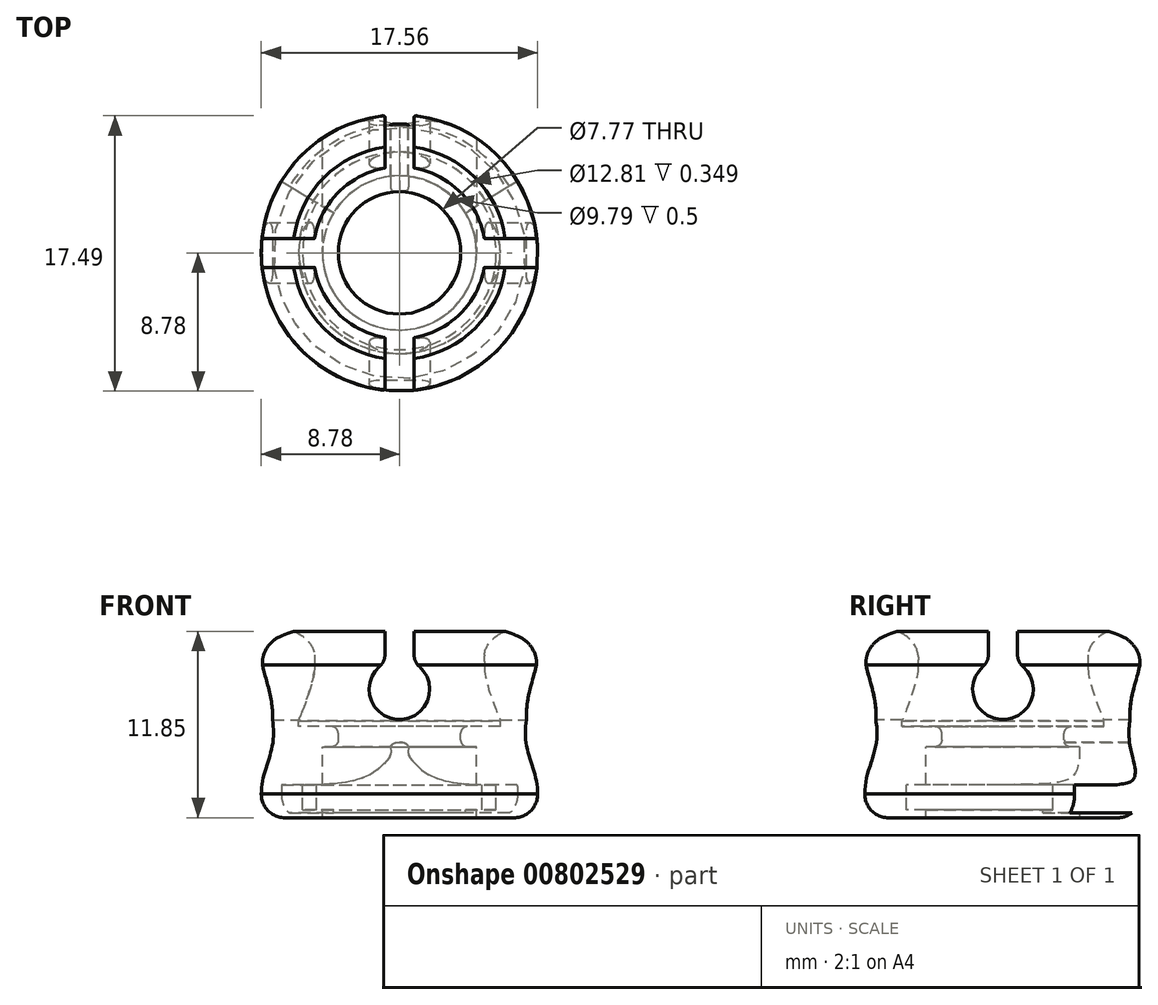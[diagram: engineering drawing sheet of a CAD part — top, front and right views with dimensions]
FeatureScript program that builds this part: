
annotation { "Feature Type Name" : "Feature", "Feature Type Description" : "" }
export const myFeature = defineFeature(function(context is Context, id is Id, definition is map)
    precondition{}
    {
        {
            var Q0;
            Q0=qCreatedBy(makeId("Front.planeOp"),FACE);
            var sketch = newSketch(context, id + "F0", { "sketchPlane" : qUnion([Q0])});
            skLineSegment(sketch, "E0", {"start": v(-3.88, 3.25) * mm, "end": v(-3.88, 2.85) * mm});
            skLineSegment(sketch, "E1", {"start": v(-4.34, 2.4) * mm, "end": v(-4.9, 2.4) * mm});
            skLineSegment(sketch, "E2", {"start": v(-4.9, 2.4) * mm, "end": v(-4.9, 0) * mm});
            skLineSegment(sketch, "E3", {"start": v(-4.9, 0) * mm, "end": v(-6.14, 0) * mm});
            skLineSegment(sketch, "E4", {"start": v(-6.14, 0) * mm, "end": v(-6.14, -1.6) * mm});
            skLineSegment(sketch, "E5", {"start": v(-6.14, -1.6) * mm, "end": v(-4.9, -1.6) * mm});
            skLineSegment(sketch, "E6", {"start": v(-4.9, -1.6) * mm, "end": v(-4.9, -2.1) * mm});
            skLineSegment(sketch, "E7", {"start": v(-4.9, -2.1) * mm, "end": v(-7.28, -2.1) * mm});
            skLineSegment(sketch, "E8", {"start": v(-8.78, -0.6) * mm, "end": v(-8.78, -0.6) * mm});
            skLineSegment(sketch, "E9", {"start": v(-7.47, 9.5) * mm, "end": v(-6.77, 9.75) * mm});
            skLineSegment(sketch, "E10", {"start": v(0, 14.29) * mm, "end": v(0, -15.3) * mm, "construction": true});
            skLineSegment(sketch, "E11", {"start": v(-6.4, 4.05) * mm, "end": v(-6.4, 3.7) * mm});
            skLineSegment(sketch, "E12", {"start": v(-6.4, 3.7) * mm, "end": v(-4.34, 3.7) * mm});
            skPoint(sketch, "E13.visualSharp", {"position": v(-8.78, 9) * mm});
            skArc(sketch, "E13.filletArc", {"start": v(-7.47, 9.5) * mm, "mid": v(-8.42, 8.76) * mm, "end": v(-8.78, 7.62) * mm});
            skPoint(sketch, "E14.visualSharp", {"position": v(-8.78, -2.1) * mm});
            skArc(sketch, "E14.filletArc", {"start": v(-8.78, -0.6) * mm, "mid": v(-8.34, -1.66) * mm, "end": v(-7.28, -2.1) * mm});
            skFitSpline(sketch, "E15", {"points": [v(-8.77, 7.62) * mm, v(-8, 3.1) * mm, v(-8.77, -0.6) * mm], "startDerivative": vector(0.2, -7.43) * mm, "endDerivative": vector(0.17, -8.43) * mm});
            skPoint(sketch, "E16.2.internal.snap0", {"position": v(-5.95, 7.8) * mm});
            skFitSpline(sketch, "E16", {"points": [v(-6.77, 9.75) * mm, v(-5.5, 8.43) * mm, v(-5.95, 6.2) * mm, v(-6.4, 4.05) * mm], "startDerivative": vector(5.68, -2.33) * mm, "endDerivative": vector(-0.9, -5.9) * mm});
            skPoint(sketch, "E17.orphan", {"position": v(-6.4, 7.18) * mm});
            skPoint(sketch, "E18.visualSharp", {"position": v(-3.88, 3.7) * mm});
            skArc(sketch, "E18.filletArc", {"start": v(-3.88, 3.25) * mm, "mid": v(-4.02, 3.57) * mm, "end": v(-4.34, 3.7) * mm});
            skPoint(sketch, "E19.visualSharp", {"position": v(-3.88, 2.4) * mm});
            skArc(sketch, "E19.filletArc", {"start": v(-4.34, 2.4) * mm, "mid": v(-4.02, 2.53) * mm, "end": v(-3.88, 2.85) * mm});
            skSolve(sketch);
        }
        {
            var Q0;
            Q0=qSketchRegion(id+"F0",true);
            var Q1;
            Q1=sQuery(id+"F0.wireOp",EDGE,"E10");
            revolve(context, id + "F1", {"surfaceOperationType" : NewSurfaceOperationType.NEW, "entities" : qUnion([Q0]), "axis" : qUnion([Q1]), "revolveType" : RevolveType.FULL});
        }
        {
            var Q0;
            Q0=qCreatedBy(makeId("Right.planeOp"),FACE);
            var sketch = newSketch(context, id + "F2", { "sketchPlane" : qUnion([Q0])});
            skArc(sketch, "E20", {"start": v(-1.27, 7.5) * mm, "mid": v(0, 4.13) * mm, "end": v(1.27, 7.5) * mm});
            skLineSegment(sketch, "E21.top", {"start": v(-0.92, 15.11) * mm, "end": v(0.93, 15.11) * mm});
            skLineSegment(sketch, "E21.left", {"start": v(-0.92, 8.26) * mm, "end": v(-0.92, 15.11) * mm});
            skLineSegment(sketch, "E21.right", {"start": v(0.93, 8.26) * mm, "end": v(0.93, 15.11) * mm});
            skPoint(sketch, "E21.middle", {"position": v(0, 11.1) * mm});
            skPoint(sketch, "E22.orphan", {"position": v(0.93, 7.1) * mm});
            skPoint(sketch, "E23.orphan", {"position": v(-0.92, 7.1) * mm});
            skPoint(sketch, "E24.visualSharp", {"position": v(0.93, 7.74) * mm});
            skArc(sketch, "E24.filletArc", {"start": v(0.92, 8.26) * mm, "mid": v(1.01, 7.84) * mm, "end": v(1.27, 7.5) * mm});
            skPoint(sketch, "E25.visualSharp", {"position": v(-0.92, 7.74) * mm});
            skArc(sketch, "E25.filletArc", {"start": v(-1.27, 7.5) * mm, "mid": v(-1.01, 7.84) * mm, "end": v(-0.92, 8.26) * mm});
            skSolve(sketch);
        }
        {
            var Q0;
            Q0=qSketchRegion(id+"F2",true);
            extrude(context, id + "F3", {"entities" : qUnion([Q0]), "operationType" : NewBodyOperationType.REMOVE, "endBound" : BoundingType.SYMMETRIC, "oppositeDirection" : true, "depth" : 25 * mm, "offsetDistance" : 25 * mm});
        }
        {
            var Q0;
            Q0=qCreatedBy(makeId("Front.planeOp"),FACE);
            var sketch = newSketch(context, id + "F4", { "sketchPlane" : qUnion([Q0])});
            skArc(sketch, "E26", {"start": v(-1.27, 7.5) * mm, "mid": v(0, 4.13) * mm, "end": v(1.27, 7.5) * mm});
            skLineSegment(sketch, "E27.top", {"start": v(-0.92, 15.11) * mm, "end": v(0.93, 15.11) * mm});
            skLineSegment(sketch, "E27.left", {"start": v(-0.92, 8.26) * mm, "end": v(-0.92, 15.11) * mm});
            skLineSegment(sketch, "E27.right", {"start": v(0.93, 8.26) * mm, "end": v(0.93, 15.11) * mm});
            skPoint(sketch, "E27.middle", {"position": v(0, 11.1) * mm});
            skPoint(sketch, "E28.orphan", {"position": v(0.93, 7.1) * mm});
            skPoint(sketch, "E29.orphan", {"position": v(-0.92, 7.1) * mm});
            skPoint(sketch, "E30.visualSharp", {"position": v(0.93, 7.74) * mm});
            skArc(sketch, "E30.filletArc", {"start": v(0.93, 8.26) * mm, "mid": v(1.01, 7.84) * mm, "end": v(1.27, 7.5) * mm});
            skPoint(sketch, "E31.visualSharp", {"position": v(-0.92, 7.74) * mm});
            skArc(sketch, "E31.filletArc", {"start": v(-1.27, 7.5) * mm, "mid": v(-1.01, 7.84) * mm, "end": v(-0.92, 8.26) * mm});
            skSolve(sketch);
        }
        {
            var Q0;
            Q0=qSketchRegion(id+"F4",true);
            extrude(context, id + "F5", {"entities" : qUnion([Q0]), "operationType" : NewBodyOperationType.REMOVE, "endBound" : BoundingType.SYMMETRIC, "oppositeDirection" : true, "depth" : 25 * mm, "offsetDistance" : 25 * mm});
        }
        {
            var Q0;
            Q0=qCreatedBy(makeId("Front.planeOp"),FACE);
            var sketch = newSketch(context, id + "F6", { "sketchPlane" : qUnion([Q0])});
            skFitSpline(sketch, "E32", {"points": [v(-4.9, 0) * mm, v(-2.89, 0.26) * mm, v(-1.45, 0.92) * mm, v(-0.69, 1.68) * mm, v(-0.54, 2.03) * mm, v(0, 2.68) * mm], "startDerivative": vector(7.16, 0.52) * mm, "endDerivative": vector(12.5, -0.27) * mm});
            skLineSegment(sketch, "E33", {"start": v(-4.9, 0) * mm, "end": v(0, 0) * mm});
            skLineSegment(sketch, "E34", {"start": v(0, 5.3) * mm, "end": v(0, -2.76) * mm, "construction": true});
            skFitSpline(sketch, "E35.MirrorCS", {"points": [v(4.9, 0) * mm, v(2.89, 0.26) * mm, v(1.45, 0.92) * mm, v(0.69, 1.68) * mm, v(0.54, 2.03) * mm, v(0, 2.68) * mm], "startDerivative": vector(-7.16, 0.52) * mm, "endDerivative": vector(-12.5, -0.27) * mm});
            skLineSegment(sketch, "E36.MirrorCS", {"start": v(4.9, 0) * mm, "end": v(0, 0) * mm});
            skSolve(sketch);
        }
        {
            var Q0;
            Q0=qSketchRegion(id+"F6",true);
            extrude(context, id + "F7", {"entities" : qUnion([Q0]), "operationType" : NewBodyOperationType.REMOVE, "oppositeDirection" : true, "depth" : 25 * mm, "offsetDistance" : 25 * mm});
        }
        {
            var Q0;
            Q0=makeQuery(id+"F7.boolean.opBoolean","COPY",FACE,{"derivedFrom":makeQuery(id+"F7.opExtrude","SWEPT_FACE",FACE,{"disambiguationData":[OSD([sQuery(id+"F6.wireOp",EDGE,"E33"),sQuery(id+"F6.wireOp",EDGE,"E36.MirrorCS")])]})});
            var sketch = newSketch(context, id + "F8", { "sketchPlane" : qUnion([Q0])});
            skLineSegment(sketch, "E37", {"start": v(-8.24, 5) * mm, "end": v(0, 0) * mm});
            skLineSegment(sketch, "E38", {"start": v(-8.24, 5) * mm, "end": v(0, 13.4) * mm});
            skLineSegment(sketch, "E39", {"start": v(0, 18.68) * mm, "end": v(0, -2.52) * mm, "construction": true});
            skLineSegment(sketch, "E40.MirrorCS", {"start": v(8.24, 5) * mm, "end": v(0, 13.4) * mm});
            skLineSegment(sketch, "E41.MirrorCS", {"start": v(8.24, 5) * mm, "end": v(0, 0) * mm});
            skSolve(sketch);
        }
        {
            var Q0;
            Q0=qSketchRegion(id+"F8",true);
            extrude(context, id + "F9", {"entities" : qUnion([Q0]), "operationType" : NewBodyOperationType.REMOVE, "oppositeDirection" : true, "depth" : 1.8 * mm, "offsetDistance" : 25 * mm});
        }
    });
